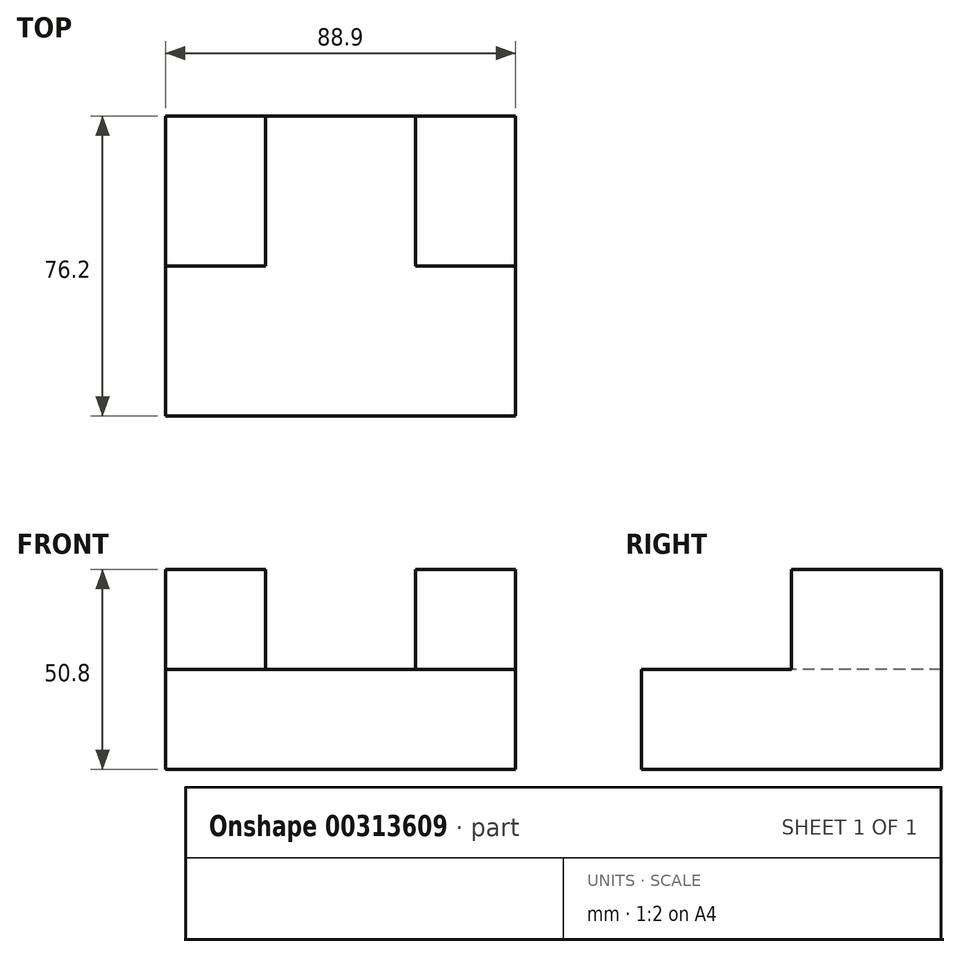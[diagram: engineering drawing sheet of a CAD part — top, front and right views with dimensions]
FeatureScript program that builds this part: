
annotation { "Feature Type Name" : "Feature", "Feature Type Description" : "" }
export const myFeature = defineFeature(function(context is Context, id is Id, definition is map)
    precondition{}
    {
        {
            var Q0;
            Q0=qCreatedBy(makeId("Front.planeOp"),FACE);
            var sketch = newSketch(context, id + "F0", { "sketchPlane" : qUnion([Q0])});
            skLineSegment(sketch, "E0", {"start": v(-49.84, -55.04) * mm, "end": v(39.06, -55.04) * mm});
            skLineSegment(sketch, "E1", {"start": v(39.06, -55.04) * mm, "end": v(39.06, -29.64) * mm});
            skLineSegment(sketch, "E2", {"start": v(39.06, -29.64) * mm, "end": v(-49.84, -29.64) * mm});
            skLineSegment(sketch, "E3", {"start": v(-49.84, -29.64) * mm, "end": v(-49.84, -55.04) * mm});
            skSolve(sketch);
        }
        {
            var Q0;
            Q0=makeQuery(id+"F0.imprint","IMPRINT",FACE,{"disambiguationData":[TD([[makeQuery(id+"F0.imprint","IMPRINT",EDGE,{"derivedFrom":sQuery(id+"F0.wireOp",EDGE,"E0")}),1.0]])]});
            extrude(context, id + "F1", {"entities" : qUnion([Q0]), "depth" : 76.2 * mm});
        }
        {
            var Q0;
            Q0=makeQuery(id+"F1.opExtrude","SWEPT_FACE",FACE,{"disambiguationData":[OSD([sQuery(id+"F0.wireOp",EDGE,"E2")])]});
            var sketch = newSketch(context, id + "F2", { "sketchPlane" : qUnion([Q0])});
            skLineSegment(sketch, "E4", {"start": v(-49.84, -38.1) * mm, "end": v(-24.44, -38.1) * mm});
            skLineSegment(sketch, "E5", {"start": v(-24.44, -38.1) * mm, "end": v(-24.44, 0) * mm});
            skLineSegment(sketch, "E6", {"start": v(13.66, 0) * mm, "end": v(13.66, -38.1) * mm});
            skLineSegment(sketch, "E7", {"start": v(13.66, -38.1) * mm, "end": v(39.06, -38.1) * mm});
            skLineSegment(sketch, "E8", {"start": v(-24.44, 0) * mm, "end": v(13.66, 0) * mm});
            skSolve(sketch);
        }
        {
            var Q0;
            {var subQ0=sQuery(id+"F2.wireOp",EDGE,"E6");Q0=makeQuery(id+"F2.imprint","IMPRINT",FACE,{"disambiguationData":[TD([[makeQuery(id+"F2.imprint","IMPRINT",EDGE,{"derivedFrom":subQ0}),1.0]])]});}
            var Q1;
            {var subQ0=sQuery(id+"F2.wireOp",EDGE,"E4");Q1=makeQuery(id+"F2.imprint","IMPRINT",FACE,{"disambiguationData":[TD([[makeQuery(id+"F2.imprint","IMPRINT",EDGE,{"derivedFrom":subQ0}),1.0]])]});}
            extrude(context, id + "F3", {"entities" : qUnion([Q0, Q1]), "operationType" : NewBodyOperationType.ADD, "depth" : 25.4 * mm});
        }
    });
